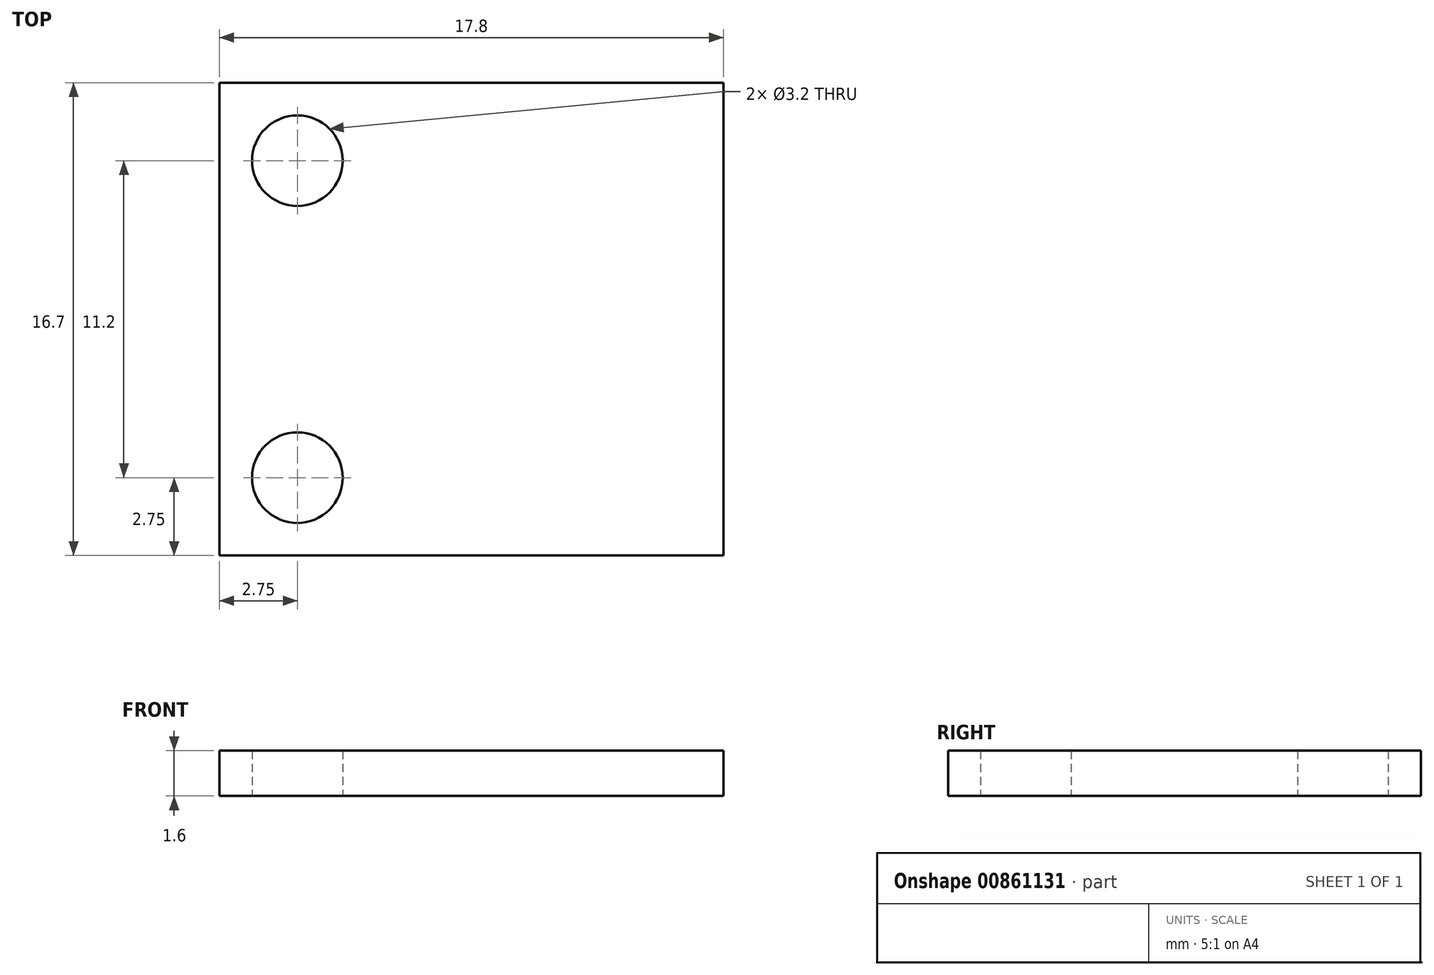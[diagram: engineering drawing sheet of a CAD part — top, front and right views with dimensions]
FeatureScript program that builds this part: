
annotation { "Feature Type Name" : "Feature", "Feature Type Description" : "" }
export const myFeature = defineFeature(function(context is Context, id is Id, definition is map)
    precondition{}
    {
        {
            var Q0;
            Q0=qCreatedBy(makeId("Top.planeOp"),FACE);
            var sketch = newSketch(context, id + "F0", { "sketchPlane" : qUnion([Q0])});
            skLineSegment(sketch, "E0.bottom", {"start": v(-8.9, 8.35) * mm, "end": v(8.9, 8.35) * mm});
            skLineSegment(sketch, "E0.top", {"start": v(-8.9, -8.35) * mm, "end": v(8.9, -8.35) * mm});
            skLineSegment(sketch, "E0.left", {"start": v(-8.9, 8.35) * mm, "end": v(-8.9, -8.35) * mm});
            skLineSegment(sketch, "E0.right", {"start": v(8.9, 8.35) * mm, "end": v(8.9, -8.35) * mm});
            skCircle(sketch, "E1", {"center": v(-6.15, 5.6) * mm, "radius": 1.6 * mm});
            skCircle(sketch, "E2", {"center": v(-6.15, -5.6) * mm, "radius": 1.6 * mm});
            skLineSegment(sketch, "E3", {"start": v(-8.9, 8.35) * mm, "end": v(-6.15, 5.6) * mm, "construction": true});
            skSolve(sketch);
        }
        {
            var Q0;
            Q0=makeQuery(id+"F0.imprint","IMPRINT",FACE,{"disambiguationData":[TD([[makeQuery(id+"F0.imprint","IMPRINT",EDGE,{"derivedFrom":sQuery(id+"F0.wireOp",EDGE,"E0.bottom")}),-1.0]])]});
            extrude(context, id + "F1", {"entities" : qUnion([Q0]), "depth" : 1.6 * mm, "offsetDistance" : 25 * mm});
        }
    });
